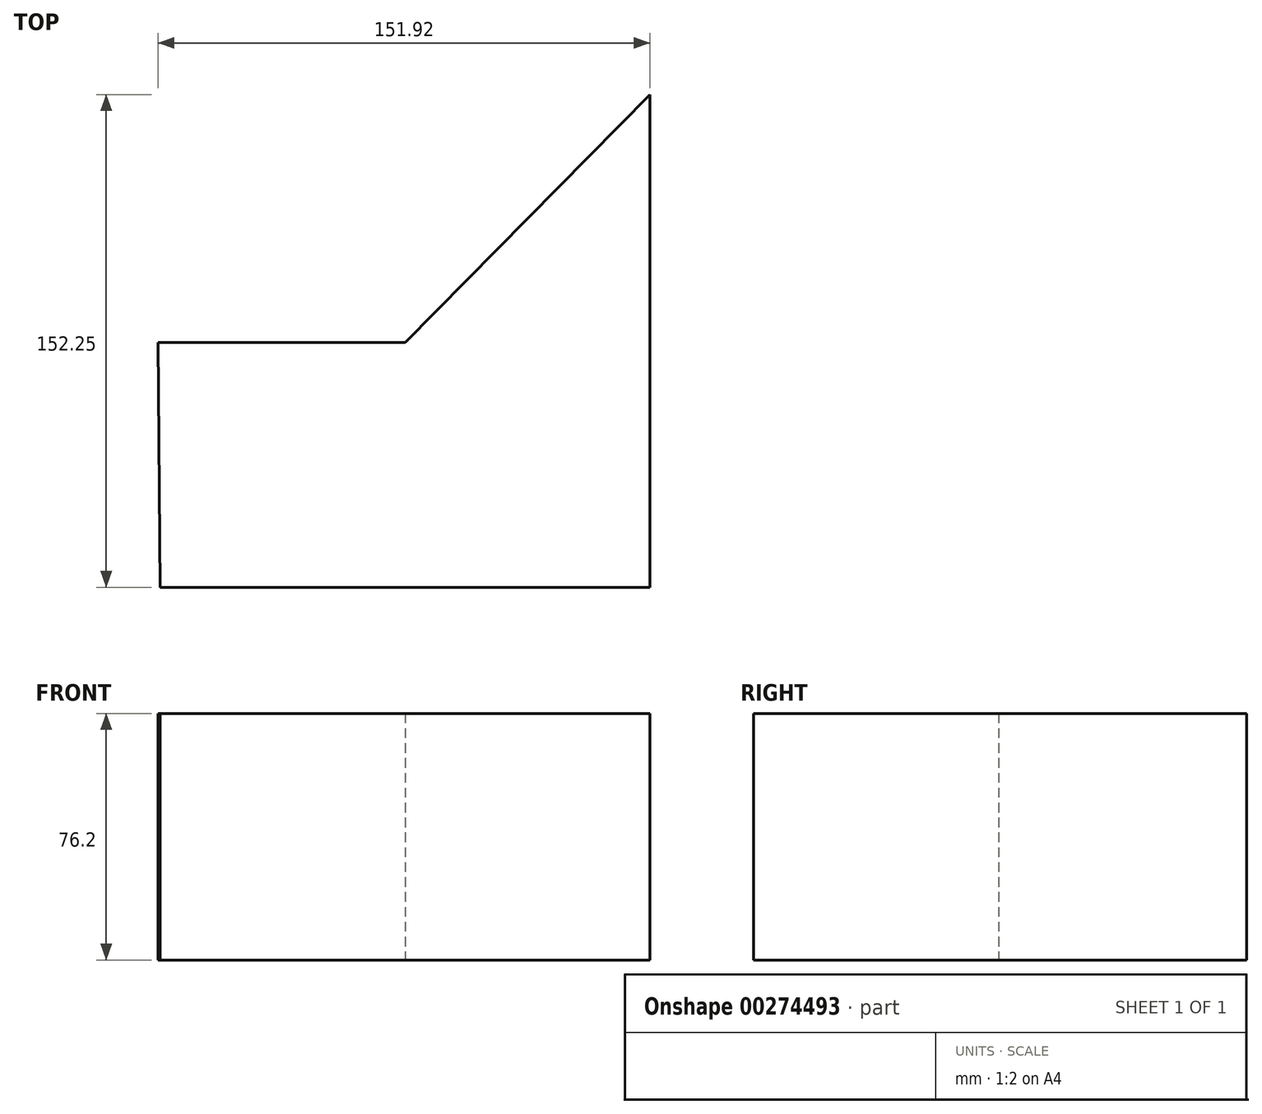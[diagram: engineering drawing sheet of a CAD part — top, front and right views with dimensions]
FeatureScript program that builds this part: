
annotation { "Feature Type Name" : "Feature", "Feature Type Description" : "" }
export const myFeature = defineFeature(function(context is Context, id is Id, definition is map)
    precondition{}
    {
        {
            var Q0;
            Q0=qCreatedBy(makeId("Top.planeOp"),FACE);
            var sketch = newSketch(context, id + "F0", { "sketchPlane" : qUnion([Q0])});
            skLineSegment(sketch, "E0", {"start": v(-76.3, 0) * mm, "end": v(0, 0) * mm});
            skLineSegment(sketch, "E1", {"start": v(0, 0) * mm, "end": v(75.62, 76.63) * mm});
            skLineSegment(sketch, "E2", {"start": v(75.62, 76.63) * mm, "end": v(75.62, -75.62) * mm});
            skLineSegment(sketch, "E3", {"start": v(75.62, -75.62) * mm, "end": v(-75.62, -75.62) * mm});
            skLineSegment(sketch, "E4", {"start": v(-75.62, -75.62) * mm, "end": v(-76.3, 0) * mm});
            skSolve(sketch);
        }
        {
            var Q0;
            Q0 = qSketchRegion(id + "F0", true);
            extrude(context, id + "F1", {"entities" : qUnion([Q0]), "depth" : 76.2 * mm});
        }
    });
